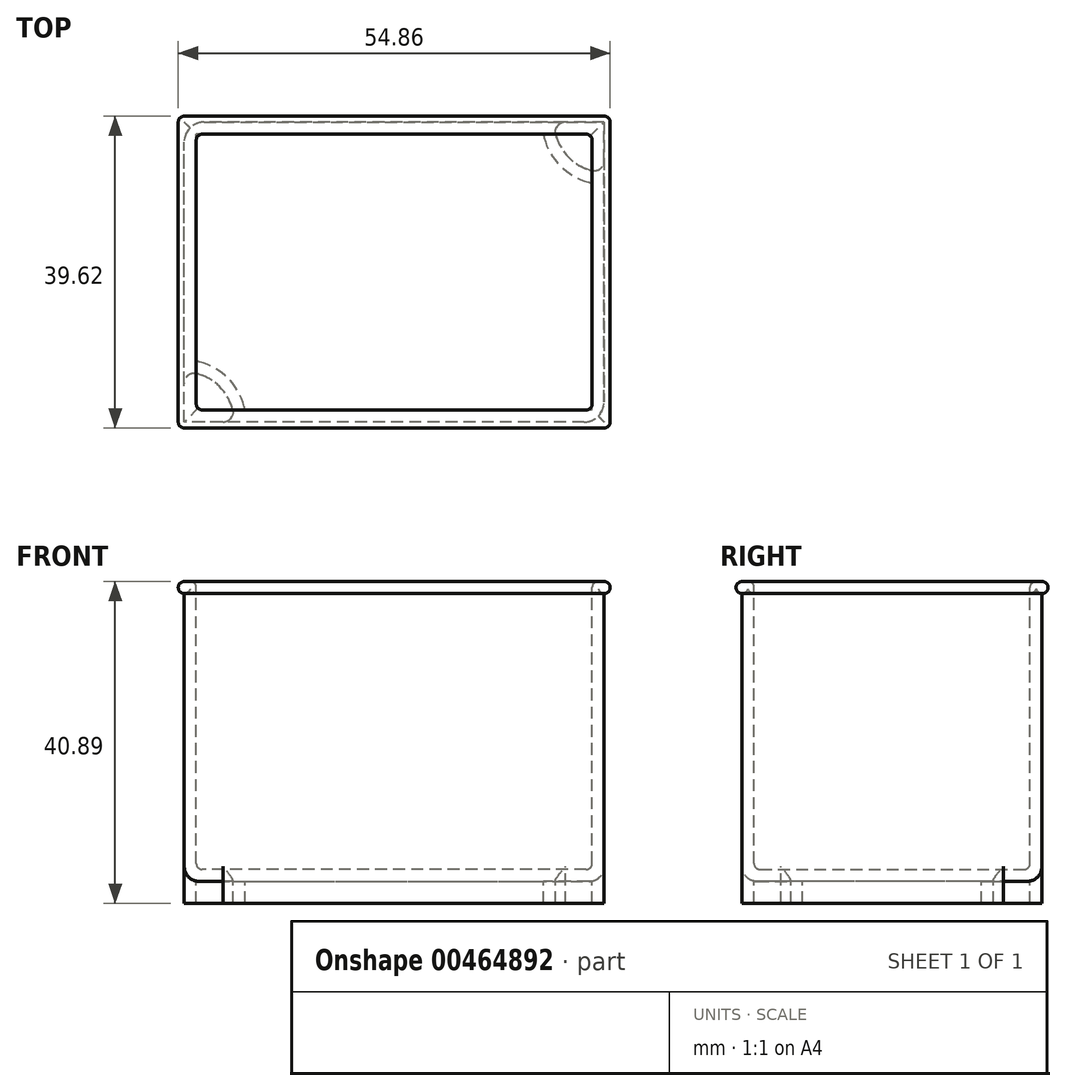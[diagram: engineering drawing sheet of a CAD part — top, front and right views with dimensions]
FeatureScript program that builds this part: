
annotation { "Feature Type Name" : "Feature", "Feature Type Description" : "" }
export const myFeature = defineFeature(function(context is Context, id is Id, definition is map)
    precondition{}
    {
        {
            var Q0;
            Q0=qCreatedBy(makeId("Front.planeOp"),FACE);
            var sketch = newSketch(context, id + "F0", { "sketchPlane" : qUnion([Q0])});
            skLineSegment(sketch, "E0.bottom", {"start": v(26.67, -19.05) * mm, "end": v(-26.67, -19.05) * mm});
            skLineSegment(sketch, "E0.top", {"start": v(26.67, 19.05) * mm, "end": v(-26.67, 19.05) * mm});
            skLineSegment(sketch, "E0.left", {"start": v(26.67, -19.05) * mm, "end": v(26.67, 19.05) * mm});
            skLineSegment(sketch, "E0.right", {"start": v(-26.67, -19.05) * mm, "end": v(-26.67, 19.05) * mm});
            skPoint(sketch, "E0.middle", {"position": v(0, 0) * mm});
            skSolve(sketch);
        }
        {
            var Q0;
            Q0=makeQuery(id+"F0.imprint","IMPRINT",FACE,{"disambiguationData":[TD([[makeQuery(id+"F0.imprint","IMPRINT",EDGE,{"derivedFrom":sQuery(id+"F0.wireOp",EDGE,"E0.bottom")}),-1.0]])]});
            extrude(context, id + "F1", {"entities" : qUnion([Q0]), "endBound" : BoundingType.SYMMETRIC, "depth" : 38.1 * mm});
        }
        {
            var Q0;
            Q0=makeQuery(id+"F1.opExtrude","SWEPT_FACE",FACE,{"disambiguationData":[OSD([sQuery(id+"F0.wireOp",EDGE,"E0.top")])]});
            shell(context, id + "F2", {"entities" : qUnion([Q0]), "thickness" : 1.52 * mm});
        }
        {
            var Q0;
            Q0=makeQuery(id+"F1.opExtrude","CAP_FACE",FACE,{"disambiguationData":[OSD([sQuery(id+"F0.wireOp",EDGE,"E0.bottom"),sQuery(id+"F0.wireOp",EDGE,"E0.top"),sQuery(id+"F0.wireOp",EDGE,"E0.left"),sQuery(id+"F0.wireOp",EDGE,"E0.right")])],"isStart":false});
            var sketch = newSketch(context, id + "F3", { "sketchPlane" : qUnion([Q0])});
            skArc(sketch, "E1", {"start": v(-26.67, 19.05) * mm, "mid": v(-27.43, 18.29) * mm, "end": v(-26.67, 17.53) * mm});
            skSolve(sketch);
        }
        {
            var Q0;
            {var subQ0=sQuery(id+"F3.wireOp",EDGE,"E1");Q0=makeQuery(id+"F3.imprint","IMPRINT",FACE,{"disambiguationData":[TD([[makeQuery(id+"F3.imprint","IMPRINT",EDGE,{"derivedFrom":subQ0}),1.0]])]});}
            var Q1;
            Q1=makeQuery(id+"F1.opExtrude","SWEPT_EDGE",EDGE,{"disambiguationData":[OSD([sQuery(id+"F0.wireOp",EDGE,"E0.top"),sQuery(id+"F0.wireOp",EDGE,"E0.right")])]});
            var Q2;
            Q2=makeQuery(id+"F1.opExtrude","CAP_EDGE",EDGE,{"disambiguationData":[OSD([sQuery(id+"F0.wireOp",EDGE,"E0.top")])],"isStart":true});
            var Q3;
            Q3=makeQuery(id+"F1.opExtrude","SWEPT_EDGE",EDGE,{"disambiguationData":[OSD([sQuery(id+"F0.wireOp",EDGE,"E0.top"),sQuery(id+"F0.wireOp",EDGE,"E0.left")])]});
            var Q4;
            Q4=makeQuery(id+"F1.opExtrude","CAP_EDGE",EDGE,{"disambiguationData":[OSD([sQuery(id+"F0.wireOp",EDGE,"E0.top")])],"isStart":false});
            sweep(context, id + "F4", {"operationType" : NewBodyOperationType.ADD, "profiles" : qUnion([Q0]), "path" : qUnion([Q1, Q2, Q3, Q4])});
        }
        {
            var Q0;
            Q0=makeQuery(id+"F1.opExtrude","SWEPT_FACE",FACE,{"disambiguationData":[OSD([sQuery(id+"F0.wireOp",EDGE,"E0.bottom")])]});
            var sketch = newSketch(context, id + "F5", { "sketchPlane" : qUnion([Q0])});
            skLineSegment(sketch, "E2.bottom", {"start": v(26.67, 19.05) * mm, "end": v(21.75, 19.05) * mm});
            skLineSegment(sketch, "E2.left", {"start": v(26.67, 19.05) * mm, "end": v(26.67, 14.13) * mm});
            skPoint(sketch, "E3.newPointA", {"position": v(20.32, 19.05) * mm});
            skArc(sketch, "E4", {"start": v(20.52, 17.46) * mm, "mid": v(22.18, 14.56) * mm, "end": v(25.08, 12.9) * mm});
            skArc(sketch, "E5.filletArc", {"start": v(21.75, 19.05) * mm, "mid": v(20.75, 18.56) * mm, "end": v(20.52, 17.46) * mm});
            skPoint(sketch, "E6.visualSharp", {"position": v(26.67, 12.7) * mm});
            skArc(sketch, "E6.filletArc", {"start": v(25.08, 12.9) * mm, "mid": v(26.18, 13.13) * mm, "end": v(26.67, 14.13) * mm});
            skArc(sketch, "E7.MirrorCS", {"start": v(-21.75, 19.05) * mm, "mid": v(-20.75, 18.56) * mm, "end": v(-20.52, 17.46) * mm});
            skArc(sketch, "E8.MirrorCS", {"start": v(-20.52, 17.46) * mm, "mid": v(-22.18, 14.56) * mm, "end": v(-25.08, 12.9) * mm});
            skArc(sketch, "E9.MirrorCS", {"start": v(-25.08, 12.9) * mm, "mid": v(-26.18, 13.13) * mm, "end": v(-26.67, 14.13) * mm});
            skLineSegment(sketch, "E10.MirrorCS", {"start": v(-26.67, 19.05) * mm, "end": v(-26.67, 14.13) * mm});
            skLineSegment(sketch, "E11.MirrorCS", {"start": v(-26.67, 19.05) * mm, "end": v(-21.75, 19.05) * mm});
            skArc(sketch, "E12.MirrorCS", {"start": v(-20.52, -17.46) * mm, "mid": v(-22.18, -14.56) * mm, "end": v(-25.08, -12.9) * mm});
            skArc(sketch, "E13.MirrorCS", {"start": v(-21.75, -19.05) * mm, "mid": v(-20.75, -18.56) * mm, "end": v(-20.52, -17.46) * mm});
            skLineSegment(sketch, "E14.MirrorCS", {"start": v(-26.67, -19.05) * mm, "end": v(-21.75, -19.05) * mm});
            skLineSegment(sketch, "E15.MirrorCS", {"start": v(-26.67, -19.05) * mm, "end": v(-26.67, -14.13) * mm});
            skArc(sketch, "E16.MirrorCS", {"start": v(-25.08, -12.9) * mm, "mid": v(-26.18, -13.13) * mm, "end": v(-26.67, -14.13) * mm});
            skArc(sketch, "E17.MirrorCS", {"start": v(21.75, -19.05) * mm, "mid": v(20.75, -18.56) * mm, "end": v(20.52, -17.46) * mm});
            skArc(sketch, "E18.MirrorCS", {"start": v(20.52, -17.46) * mm, "mid": v(22.18, -14.56) * mm, "end": v(25.08, -12.9) * mm});
            skArc(sketch, "E19.MirrorCS", {"start": v(25.08, -12.9) * mm, "mid": v(26.18, -13.13) * mm, "end": v(26.67, -14.13) * mm});
            skLineSegment(sketch, "E20.MirrorCS", {"start": v(26.67, -19.05) * mm, "end": v(26.67, -14.13) * mm});
            skLineSegment(sketch, "E21.MirrorCS", {"start": v(26.67, -19.05) * mm, "end": v(21.75, -19.05) * mm});
            skSolve(sketch);
        }
        {
            var Q0;
            Q0=makeQuery(id+"F5.imprint","IMPRINT",FACE,{"disambiguationData":[TD([[makeQuery(id+"F5.imprint","IMPRINT",EDGE,{"derivedFrom":sQuery(id+"F5.wireOp",EDGE,"E2.bottom")}),1.0]])]});
            var Q1;
            Q1=makeQuery(id+"F5.imprint","IMPRINT",FACE,{"disambiguationData":[TD([[makeQuery(id+"F5.imprint","IMPRINT",EDGE,{"derivedFrom":sQuery(id+"F5.wireOp",EDGE,"E8.MirrorCS")}),-1.0]])]});
            var Q2;
            Q2=makeQuery(id+"F5.imprint","IMPRINT",FACE,{"disambiguationData":[TD([[makeQuery(id+"F5.imprint","IMPRINT",EDGE,{"derivedFrom":sQuery(id+"F5.wireOp",EDGE,"E12.MirrorCS")}),1.0]])]});
            var Q3;
            Q3=makeQuery(id+"F5.imprint","IMPRINT",FACE,{"disambiguationData":[TD([[makeQuery(id+"F5.imprint","IMPRINT",EDGE,{"derivedFrom":sQuery(id+"F5.wireOp",EDGE,"E17.MirrorCS")}),-1.0]])]});
            extrude(context, id + "F6", {"entities" : qUnion([Q0, Q1, Q2, Q3]), "operationType" : NewBodyOperationType.ADD, "depth" : 2.8 * mm});
        }
        {
            var Q0;
            Q0=makeQuery(id+"F6.opExtrude","CAP_FACE",FACE,{"disambiguationData":[OSD([sQuery(id+"F5.wireOp",EDGE,"E2.bottom"),sQuery(id+"F5.wireOp",EDGE,"E2.left"),sQuery(id+"F5.wireOp",EDGE,"E4"),sQuery(id+"F5.wireOp",EDGE,"E5.filletArc"),sQuery(id+"F5.wireOp",EDGE,"E6.filletArc")])],"isStart":false});
            var Q1;
            Q1=makeQuery(id+"F6.opExtrude","CAP_FACE",FACE,{"disambiguationData":[OSD([sQuery(id+"F5.wireOp",EDGE,"E8.MirrorCS"),sQuery(id+"F5.wireOp",EDGE,"E9.MirrorCS"),sQuery(id+"F5.wireOp",EDGE,"E10.MirrorCS"),sQuery(id+"F5.wireOp",EDGE,"E7.MirrorCS"),sQuery(id+"F5.wireOp",EDGE,"E11.MirrorCS")])],"isStart":false});
            var Q2;
            Q2=makeQuery(id+"F6.opExtrude","CAP_FACE",FACE,{"disambiguationData":[OSD([sQuery(id+"F5.wireOp",EDGE,"E12.MirrorCS"),sQuery(id+"F5.wireOp",EDGE,"E13.MirrorCS"),sQuery(id+"F5.wireOp",EDGE,"E14.MirrorCS"),sQuery(id+"F5.wireOp",EDGE,"E15.MirrorCS"),sQuery(id+"F5.wireOp",EDGE,"E16.MirrorCS")])],"isStart":false});
            var Q3;
            Q3=makeQuery(id+"F6.opExtrude","CAP_FACE",FACE,{"disambiguationData":[OSD([sQuery(id+"F5.wireOp",EDGE,"E17.MirrorCS"),sQuery(id+"F5.wireOp",EDGE,"E18.MirrorCS"),sQuery(id+"F5.wireOp",EDGE,"E19.MirrorCS"),sQuery(id+"F5.wireOp",EDGE,"E20.MirrorCS"),sQuery(id+"F5.wireOp",EDGE,"E21.MirrorCS")])],"isStart":false});
            shell(context, id + "F7", {"entities" : qUnion([Q0, Q1, Q2, Q3]), "thickness" : 1.52 * mm});
        }
        {
            var Q0;
            Q0=makeQuery(id+"F2.opShell","OFFSET_FACE",FACE,{"disambiguationData":[OSD([sQuery(id+"F0.wireOp",EDGE,"E0.left")])]});
            var Q1;
            {var subQ0=sQuery(id+"F0.wireOp",EDGE,"E0.right");var subQ1=sQuery(id+"F0.wireOp",EDGE,"E0.left");var subQ2=sQuery(id+"F0.wireOp",EDGE,"E0.top");var subQ3=sQuery(id+"F0.wireOp",EDGE,"E0.bottom");Q1=makeQuery(id+"F2.opShell","OFFSET_FACE",FACE,{"disambiguationData":[OSD([subQ3,subQ2,subQ1,subQ0]),TDD([makeQuery(id+"F1.opExtrude","CAP_FACE",FACE,{"disambiguationData":[OSD([subQ3,subQ2,subQ1,subQ0])],"isStart":true})])]});}
            var Q2;
            Q2=makeQuery(id+"F2.opShell","OFFSET_FACE",FACE,{"disambiguationData":[OSD([sQuery(id+"F0.wireOp",EDGE,"E0.right")])]});
            var Q3;
            {var subQ0=sQuery(id+"F0.wireOp",EDGE,"E0.right");var subQ1=sQuery(id+"F0.wireOp",EDGE,"E0.left");var subQ2=sQuery(id+"F0.wireOp",EDGE,"E0.top");var subQ3=sQuery(id+"F0.wireOp",EDGE,"E0.bottom");Q3=makeQuery(id+"F2.opShell","OFFSET_FACE",FACE,{"disambiguationData":[OSD([subQ3,subQ2,subQ1,subQ0]),TDD([makeQuery(id+"F1.opExtrude","CAP_FACE",FACE,{"disambiguationData":[OSD([subQ3,subQ2,subQ1,subQ0])],"isStart":false})])]});}
            fillet(context, id + "F8", {"entities" : qUnion([Q0, Q1, Q2, Q3]), "radius" : 0.76 * mm, "tangentPropagation" : true, "allowEdgeOverflow" : false});
        }
        {
            var Q0;
            Q0=makeQuery(id+"F1.opExtrude","SWEPT_EDGE",EDGE,{"disambiguationData":[OSD([sQuery(id+"F0.wireOp",EDGE,"E0.bottom"),sQuery(id+"F0.wireOp",EDGE,"E0.right")])]});
            var Q1;
            Q1=makeQuery(id+"F1.opExtrude","CAP_EDGE",EDGE,{"disambiguationData":[OSD([sQuery(id+"F0.wireOp",EDGE,"E0.bottom")])],"isStart":false});
            var Q2;
            Q2=makeQuery(id+"F1.opExtrude","SWEPT_EDGE",EDGE,{"disambiguationData":[OSD([sQuery(id+"F0.wireOp",EDGE,"E0.bottom"),sQuery(id+"F0.wireOp",EDGE,"E0.left")])]});
            var Q3;
            Q3=makeQuery(id+"F1.opExtrude","CAP_EDGE",EDGE,{"disambiguationData":[OSD([sQuery(id+"F0.wireOp",EDGE,"E0.bottom")])],"isStart":true});
            fillet(context, id + "F9", {"entities" : qUnion([Q0, Q1, Q2, Q3]), "radius" : 1.9 * mm, "tangentPropagation" : true, "allowEdgeOverflow" : false});
        }
        {
            var Q0;
            Q0=makeQuery(id+"F4.opSweep","MID_CAP_EDGE",EDGE,{"disambiguationData":[OSD([sQuery(id+"F0.wireOp",EDGE,"E0.top"),sQuery(id+"F0.wireOp",EDGE,"E0.left"),sQuery(id+"F3.wireOp",EDGE,"E1")])],"capPos":3.0});
            var Q1;
            Q1=makeQuery(id+"F4.opSweep","MID_CAP_EDGE",EDGE,{"disambiguationData":[OSD([sQuery(id+"F0.wireOp",EDGE,"E0.top"),sQuery(id+"F0.wireOp",EDGE,"E0.left"),sQuery(id+"F3.wireOp",EDGE,"E1")])],"capPos":2.0});
            var Q2;
            Q2=makeQuery(id+"F4.opSweep","MID_CAP_EDGE",EDGE,{"disambiguationData":[OSD([sQuery(id+"F0.wireOp",EDGE,"E0.top"),sQuery(id+"F0.wireOp",EDGE,"E0.right"),sQuery(id+"F3.wireOp",EDGE,"E1")])],"capPos":1.0});
            var Q3;
            Q3=makeQuery(id+"F4.opSweep","CAP_EDGE",EDGE,{"disambiguationData":[OSD([sQuery(id+"F0.wireOp",EDGE,"E0.top"),sQuery(id+"F0.wireOp",EDGE,"E0.right"),sQuery(id+"F3.wireOp",EDGE,"E1")])],"isStart":true});
            fillet(context, id + "F10", {"entities" : qUnion([Q0, Q1, Q2, Q3]), "radius" : 0.76 * mm, "tangentPropagation" : true, "allowEdgeOverflow" : false});
        }
        {
            var Q0;
            Q0=makeQuery(id+"F6.boolean.opBoolean","MERGE",EDGE,{"derivedFrom":[makeQuery(id+"F1.opExtrude","CAP_EDGE",EDGE,{"disambiguationData":[OSD([sQuery(id+"F0.wireOp",EDGE,"E0.left")])],"isStart":false}),makeQuery(id+"F6.opExtrude","SWEPT_EDGE",EDGE,{"disambiguationData":[OSD([sQuery(id+"F5.wireOp",EDGE,"E2.bottom"),sQuery(id+"F5.wireOp",EDGE,"E2.left")])]})]});
            var Q1;
            Q1=makeQuery(id+"F6.boolean.opBoolean","MERGE",EDGE,{"derivedFrom":[makeQuery(id+"F1.opExtrude","CAP_EDGE",EDGE,{"disambiguationData":[OSD([sQuery(id+"F0.wireOp",EDGE,"E0.left")])],"isStart":true}),makeQuery(id+"F6.opExtrude","SWEPT_EDGE",EDGE,{"disambiguationData":[OSD([sQuery(id+"F5.wireOp",EDGE,"E20.MirrorCS"),sQuery(id+"F5.wireOp",EDGE,"E21.MirrorCS")])]})]});
            var Q2;
            Q2=makeQuery(id+"F6.boolean.opBoolean","MERGE",EDGE,{"derivedFrom":[makeQuery(id+"F1.opExtrude","CAP_EDGE",EDGE,{"disambiguationData":[OSD([sQuery(id+"F0.wireOp",EDGE,"E0.right")])],"isStart":false}),makeQuery(id+"F6.opExtrude","SWEPT_EDGE",EDGE,{"disambiguationData":[OSD([sQuery(id+"F5.wireOp",EDGE,"E10.MirrorCS"),sQuery(id+"F5.wireOp",EDGE,"E11.MirrorCS")])]})]});
            var Q3;
            Q3=makeQuery(id+"F6.boolean.opBoolean","MERGE",EDGE,{"derivedFrom":[makeQuery(id+"F1.opExtrude","CAP_EDGE",EDGE,{"disambiguationData":[OSD([sQuery(id+"F0.wireOp",EDGE,"E0.right")])],"isStart":true}),makeQuery(id+"F6.opExtrude","SWEPT_EDGE",EDGE,{"disambiguationData":[OSD([sQuery(id+"F5.wireOp",EDGE,"E14.MirrorCS"),sQuery(id+"F5.wireOp",EDGE,"E15.MirrorCS")])]})]});
            fillet(context, id + "F11", {"entities" : qUnion([Q0, Q1, Q2, Q3]), "radius" : 2.54 * mm, "tangentPropagation" : true, "allowEdgeOverflow" : false});
        }
    });
